# Revit family: ТвінФреш Комфо_Eng
name_source: partatom
category: Mechanical Equipment
units: mm (PartAtom-declared; Revit-internal decimal feet)

## family parameters
Always vertical = Yes
Classification = None
Cut with Voids When Loaded = Yes
Part Type = Normal
Room Calculation Point = No
Round Connector Dimension = Use Diameter
Shared = No
Work Plane-Based = No

## types (6) — shared parameters
00_20_Manufacturer = Vents
00_20_Name = Ventilators
B = 240 mm  [stored 0.787402 ft]
B1 = 186 mm  [stored 0.610236 ft]
Casing Material = Plastic, opaque, white
D = 157 mm  [stored 0.515092 ft]
Diameter = 157 mm  [stored 0.515092 ft]
Dy = 152 mm  [stored 0.498688 ft]
Filter = G3
Frequency = 50 Hz
L = 240 mm  [stored 0.787402 ft]
L2 = 86 mm  [stored 0.282152 ft]
Load Classification = HVAC
Maintenance zone material = <By Category>
Manufacturer = Vents
Number of Fase = 1
Temperature of moving air = -20...+40 °С
URL = https://ventilation-system.com
Voltage = 230 V
Weight = 5.00 kg
b = 180 mm  [stored 0.590551 ft]
b1 = 200 mm  [stored 0.656168 ft]
l1 = 188 mm  [stored 0.616798 ft]
l2 = 126 mm
l3 = 115 mm  [stored 0.377297 ft]
zero-valued in all types: Default Elevation

## per-type parameters (varying)
| type | Amperage | Height | Length | Maximum Air Flow | Power | Sound pressure level at 3 m distance | Width | Колпак 2 | Колпак 23 |
| TwinFresh Comfo RA1-50 В.3 | 0.039 A | 240 mm  [stored 0.787402 ft] | 385 mm  [stored 1.26312 ft] | 50.0 m³/h | 7 W | 23 dBA | 240 mm  [stored 0.787402 ft] | No | No |
| TwinFresh Comfo RA1-50-2 В.3 | 0.039 A | 260 mm  [stored 0.853018 ft] | 455 mm | 50.0 m³/h | 7 W | 23 dBA | 300 mm | Yes | No |
| TwinFresh Comfo RA1-50-23 В.3 | 0.039 A | 260 mm  [stored 0.853018 ft] | 440 mm  [stored 1.44357 ft] | 50.0 m³/h | 7 W | 23 dBA | 300 mm | No | Yes |
| TwinFresh Comfo RA1-85 В.3 | 0.071 A | 240 mm  [stored 0.787402 ft] | 385 mm  [stored 1.26312 ft] | 85.0 m³/h | 10 W | 34 dBA | 240 mm  [stored 0.787402 ft] | No | No |
| TwinFresh Comfo RA1-85-2 В.3 | 0.071 A | 260 mm  [stored 0.853018 ft] | 455 mm | 85.0 m³/h | 10 W | 34 dBA | 300 mm | Yes | No |
| TwinFresh Comfo RA1-85-23 В.3 | 0.071 A | 260 mm  [stored 0.853018 ft] | 440 mm  [stored 1.44357 ft] | 85.0 m³/h | 10 W | 34 dBA | 300 mm | No | Yes |

note: column(s) folded — value = type name in every type: 00_20_Type

note: [stored X ft] marks values corroborated as IEEE doubles in the binary element streams (Revit-internal decimal feet)
